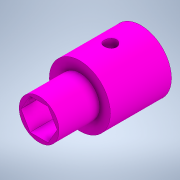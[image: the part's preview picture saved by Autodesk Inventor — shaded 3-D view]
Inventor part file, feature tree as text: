
AUTODESK INVENTOR PART (.ipt)
format: ipt  version: 2022.1 (Build 261234000, 234)  size: 155,648 bytes
history: native  units: in
note: dims shown in document units (in); Inventor stores cm internally (conversion verified against a paired STEP export)
features: sketch x3, extrude x2, other x1, thicken_offset x1, plane x1, hole x1
ambient origin geometry x8: Origin, YZ Plane, XZ Plane, XY Plane, X Axis, Y Axis, Z Axis, Center Point
bodies: Solid1 (feature_tree)
feature tree (9):
  extrude  "Extrusion1"  Depth=0.75in
  other  "Thicken Hex"
  extrude  "Extrusion2"  Depth=0.75in TaperAngle=0.0deg
  thicken_offset  "Thicken2"
  plane  "Work Plane1"
  hole  "Hole1"  [1 undecoded]
  sketch  "Sketch1"  dims[d0=0.375in d2=0.75in]
  sketch  "Sketch3"  dims[d3=0.1585in d4=0.75in d5=0.0in]
  sketch  "Sketch4"  dims[d6=0.005in d7=0.005in d8=0.5in d9=0.0in d10=0.5in d11=0.005in d12=0.005in d13=0.15in d14=0.75in d15=0.279in d16=0.25in d17=0.5635in d18=1.0in d19=0.8108in]
note: 1 required parameter value undecoded (feature->parameter linkage not recoverable at this tier; creation-order binding heuristic only, values carry confidence <= 0.55)
